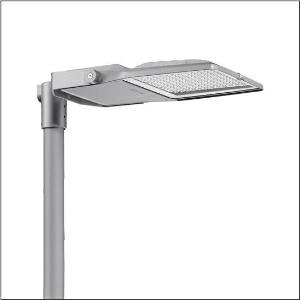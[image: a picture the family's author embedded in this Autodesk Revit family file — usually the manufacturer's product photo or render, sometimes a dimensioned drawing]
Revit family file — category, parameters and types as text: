
# Revit family: floodlight_fl_21_iq_midi___pl61_5xa7781f2c3a_20a4
name_source: partatom
category: Lighting Fixtures
units: mm (PartAtom-declared; Revit-internal decimal feet)

## family parameters
Cut with Voids When Loaded = No
Host = Face
Light Source = No
Part Type = Normal
Room Calculation Point = No
Round Connector Dimension = Use Diameter
Shared = No

## types (1)
- --- (1 x LED, 35100 lm, 270.2 W, 3000K)
    Apparent Load = 270 VA
    CIE Flux Codes = 33 65 98 100 100
    Color Rendering = 70
    Color Temperature = 3000K
    Default Elevation = 1800 mm
    Description = Floodlight FL 21 iQ midi, floodlight, primary light control with lens, of PMMA, primary optical cover: protective disc, of toughened safety glass, transparent, light distribution: PL61, light emission: direct distribution, installation type: surface-mounted, lamps: LED, High Power LED, rated values: 35.100lm | 270,2W | 129,9lm/W (begin service life); end service life: 35.100lm | 286,6W; at 50% lumin. flux: 17.550lm | 117,4W | 149,5lm/W, colour temperature: 3000K, colour rendering: CRI > 70, light colour: 730, light setting 1 begin service life: 100% | 35.100lm | 270,2W | 129,9lm/W | 3.000K, light setting 1 end service life: 286,6W, further light settings possible, control: optimised constant luminous flux control (CLO 2.0), Desk-Remote (wireless, voltage-free reading and setting of iQ features in the workshop via application-optimized NFC function/RFID function), Light-Fading, Smart-Wire, Night-Set, Lumen-Switch, Temp-Guard, Auto-Match, pre-setting: linear dimming characteristic, with terminal, 6-pole, mains connection: 220..240V, AC, 50/60Hz, luminaire housing, of diecast aluminium, powder-coated, SITECO metallic grey (DB 702S), corrosivity category C5 mid according to DIN EN ISO 12944suitable for swimming poolschlorine-resistant, sealing non-destructively replaceable, please order mast flange separately, mast bracket, of steel, galvanised, powder-coated, SITECO metallic grey (DB 702S), protection rating (complete): IP66, insulation class (complete): insulation class II (safety insulation), certification: CE, ENEC, VDE, protection symbol: D, impact resistance: IK08, permissible operating ambient temperature: -40..+40°C, permissible operating ambient temperature for outdoor applications: -40..+50°C, standard: DIN EN 12944, LABS conformity tested according to VDMA 24364:2018-05, packaging unit: 1 piece

Light Distribution: PL61
    Height = 76 mm
    Lamp = 1 x LED
    Lamp Light Flux = 35100 lm
    Lamp Power = 270.2 W
    Lamp count = 1
    Length = 657 mm
    Luminous efficacy = 130 lm/W
    Manufacturer = Siteco
    ModVariant = No
    Model = 5XA7781F2C3A
    Mounting Place = Pole
    Mounting Type = Pole annexe
    Number of Poles = 1
    OnlyDefault = Yes
    Power Factor = 1
    Product Name = Floodlight FL 21 iQ midi | PL61
    Product group = floodlight | pylon annexe
    ProductGroupID = 6201
    Protection Class = Protection class II
    Protection Degree = IP 66
    RLX_Detail_Level = 1
    RLX_Emergency_Light_Flux = 0 lm
    RLX_Emergency_Type = 0
    RLX_Emergency_Type_DB = No
    RlxData = <blob elided: 153953 chars, md5=f39d975f>
    Socket = socket
    Standby Power = 0 W
    System Light Flux = 35100 lm
    System Power = 270 W
    Type Comments = factory setting: luminous flux: 100 % | dim-lin: 254 | 620 mA
    Type Image = l_1007123.jpg
    URL = http://relux.com
    VarID = @adj_109989
    Voltage = 0 V
    Weight = 0.00 kg
    Width = 442 mm

## geometry (parser evidence)
native form markers: Blend x4, Sweep x12
no freeform markers — native parametric forms only
